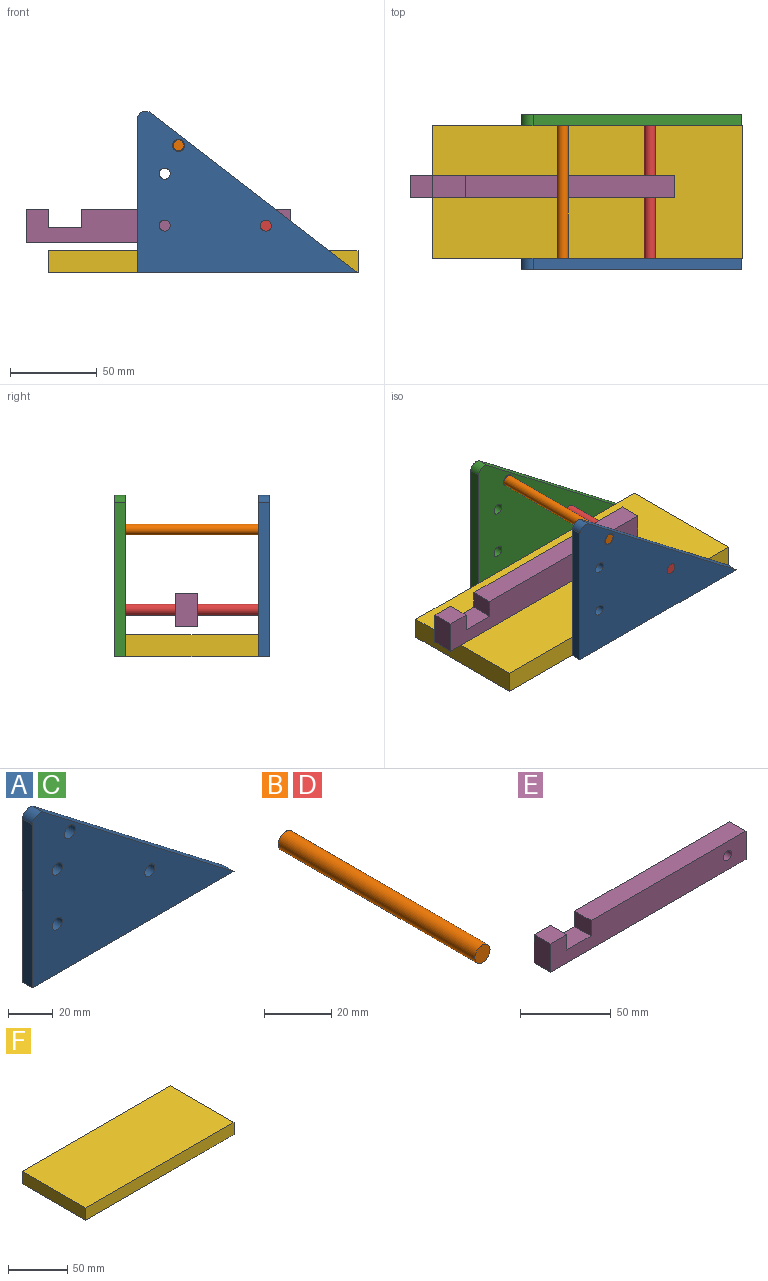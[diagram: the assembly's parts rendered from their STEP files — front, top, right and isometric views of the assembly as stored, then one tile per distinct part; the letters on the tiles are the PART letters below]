
ASSEMBLY  parts=6 mates=5
PART A: 10 faces, bbox 127x6.4x92.8 mm
  f0: cylinder r=5.08mm len=6.82mm, axis (0,1,0), area 55.5mm2, adj f1,f7,f8,f9
  f1: plane 88.9x6.35mm, normal (-1,0,0), area 564.5mm2, adj f0,f2,f8,f9
  f2: plane 127x6.35mm, normal (0,0,-1), area 806.5mm2, adj f1,f7,f8,f9
  f3: cylinder r=3.47mm len=6.95mm, axis (0,1,0), area 138.6mm2, adj f8,f9
  f4: cylinder r=3.17mm len=6.35mm, axis (0,1,0), area 126.7mm2, adj f8,f9
  f5: cylinder r=3.17mm len=6.35mm, axis (0,1,0), area 126.7mm2, adj f8,f9
  f6: cylinder r=3.17mm len=6.35mm, axis (0,1,0), area 126.7mm2, adj f8,f9
  f7: plane 120.18x92.49mm, normal (0.61,0,0.79), area 963mm2, adj f0,f2,f8,f9
  f8: plane 127x92.85mm, normal (0,-1,0), area 6052.8mm2, adj f0,f1,f2,f3,f4,f5,f6,f7
  f9: plane 127x92.85mm, normal (0,1,0), area 6052.8mm2, adj f0,f1,f2,f3,f4,f5,f6,f7
PART B: 3 faces, bbox 6.4x82.6x6.4 mm
  f0: cylinder r=3.17mm len=82.55mm, axis (0,1,0), area 1646.8mm2, adj f1,f2
  f1: plane 6.35x6.35mm, normal (0,-1,0), area 31.7mm2, adj f0
  f2: plane 6.35x6.35mm, normal (0,1,0), area 31.7mm2, adj f0
PART C: same geometry as A
PART D: same geometry as B
PART E: 11 faces, bbox 152.4x12.7x19.1 mm
  f0: plane 120.65x12.7mm, normal (0,0,1), area 1532.3mm2, adj f1,f3,f5,f7
  f1: plane 152.4x19.05mm, normal (0,1,0), area 2673.7mm2, adj f0,f2,f4,f5,f6,f7,f8,f9
  f2: plane 12.7x12.7mm, normal (0,0,1), area 161.3mm2, adj f1,f3,f6,f8
  f3: plane 152.4x19.05mm, normal (0,-1,0), area 2673.7mm2, adj f0,f2,f4,f5,f6,f7,f8,f9
  f4: plane 152.4x12.7mm, normal (0,0,-1), area 1935.5mm2, adj f1,f3,f5,f6
  f5: plane 19.05x12.7mm, normal (1,0,0), area 241.9mm2, adj f0,f1,f3,f4
  f6: plane 19.05x12.7mm, normal (-1,0,0), area 241.9mm2, adj f1,f2,f3,f4
  f7: plane 12.7x10.36mm, normal (-1,0,0), area 131.6mm2, adj f0,f1,f3,f9
  f8: plane 12.7x10.36mm, normal (1,0,0), area 131.6mm2, adj f1,f2,f3,f9
  f9: plane 19.05x12.7mm, normal (0,0,1), area 241.9mm2, adj f1,f3,f7,f8
  f10: cylinder r=3.2mm len=12.7mm, axis (0,-1,0), area 255.4mm2, adj f1,f3
PART F: 6 faces, bbox 177.8x76.2x12.7 mm
  f0: plane 177.8x12.7mm, normal (0,1,0), area 2258.1mm2, adj f1,f3,f4,f5
  f1: plane 76.2x12.7mm, normal (-1,0,0), area 967.7mm2, adj f0,f2,f4,f5
  f2: plane 177.8x12.7mm, normal (0,-1,0), area 2258.1mm2, adj f1,f3,f4,f5
  f3: plane 76.2x12.7mm, normal (1,0,0), area 967.7mm2, adj f0,f2,f4,f5
  f4: plane 177.8x76.2mm, normal (0,0,1), area 13548.4mm2, adj f0,f1,f2,f3
  f5: plane 177.8x76.2mm, normal (0,0,-1), area 13548.4mm2, adj f0,f1,f2,f3
PLACE A t=(108.83,-3.6,66.3)mm
PLACE B t=(97.92,72.6,83.1)mm
PLACE C t=(108.83,78.95,66.3)mm
PLACE D t=(148.17,72.6,36.97)mm
PLACE E t=(-3.61,35.4,20.18)mm
PLACE F t=(93.61,49.42,-6.94)mm fixed
MATE fastened C.f8 <-> F.f0  axis (0,-1,0) through (187.32,72.6,-6.94)mm
MATE slider B.f0 <-> A.f3  axis (0,-1,0) through (84.11,-9.95,66.3)mm
MATE fastened A.f9 <-> F.f2  axis (0,1,0) through (187.32,-3.6,-6.94)mm
MATE fastened D.f0 <-> E.f10  axis (0,1,0) through (134.36,31.33,20.18)mm
MATE slider D.f0 <-> A.f6  axis (0,-1,0) through (134.36,-9.95,20.18)mm
